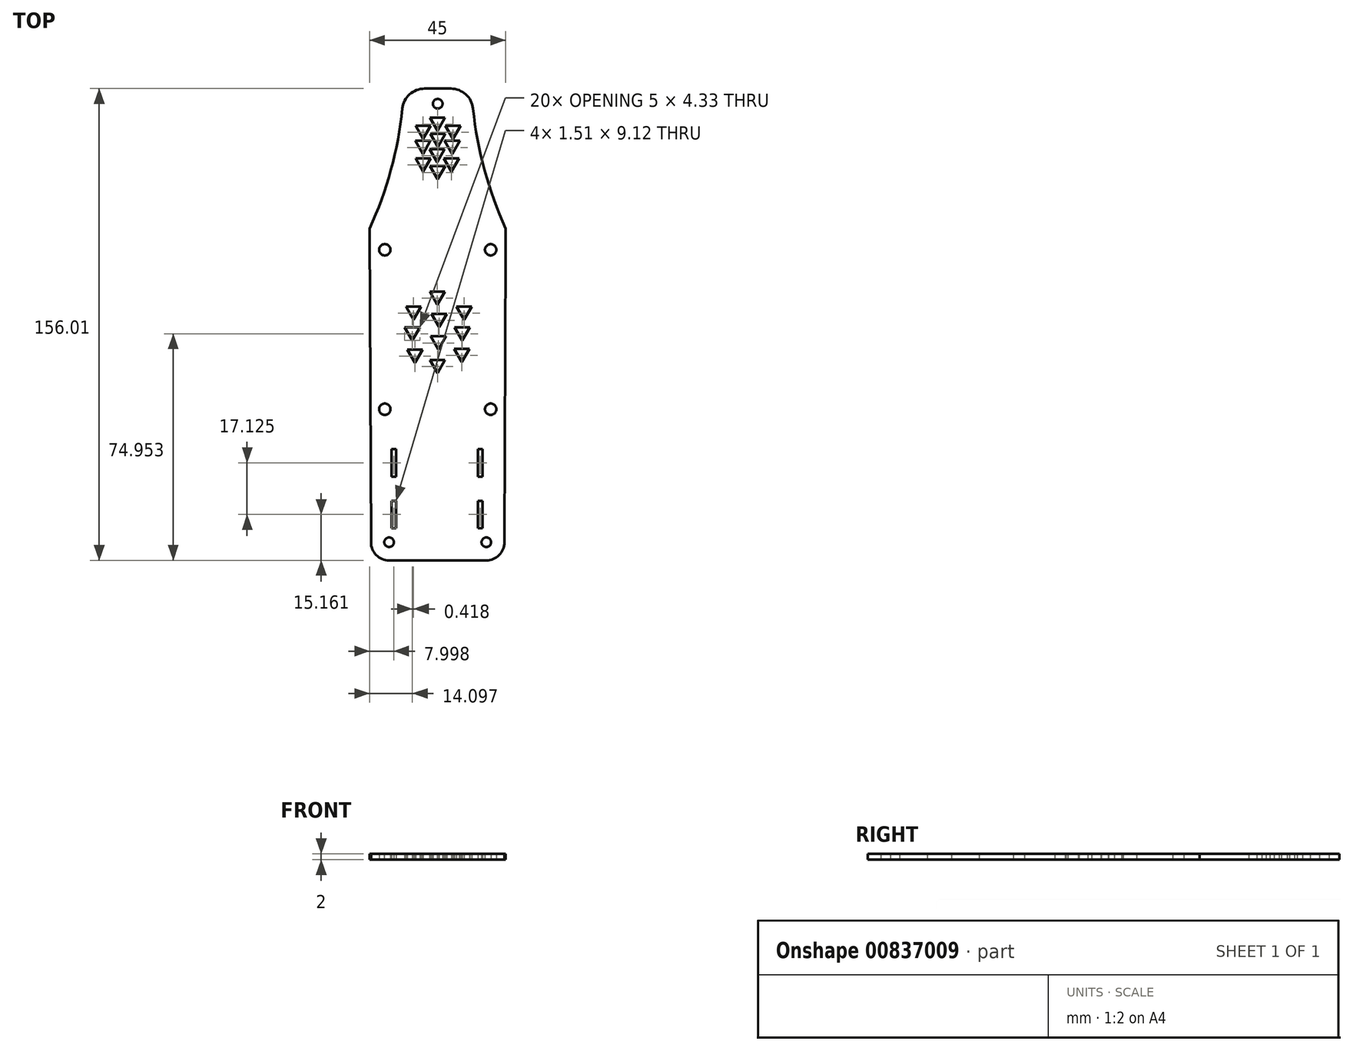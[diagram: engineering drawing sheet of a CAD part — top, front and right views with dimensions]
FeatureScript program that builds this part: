
annotation { "Feature Type Name" : "Feature", "Feature Type Description" : "" }
export const myFeature = defineFeature(function(context is Context, id is Id, definition is map)
    precondition{}
    {
        {
            var Q0;
            Q0=qCreatedBy(makeId("Top.planeOp"),FACE);
            var sketch = newSketch(context, id + "F0", { "sketchPlane" : qUnion([Q0])});
            skLineSegment(sketch, "E0.trimOffspring", {"start": v(9.73, 3.85) * mm, "end": v(9.72, 1.55) * mm});
            skArc(sketch, "E1.MirrorCS", {"start": v(-8.3, 74.97) * mm, "mid": v(-8.3, 74.97) * mm, "end": v(-8.3, 74.98) * mm});
            skLineSegment(sketch, "E2", {"start": v(-12.66, 82.35) * mm, "end": v(-8.3, 82.35) * mm});
            skLineSegment(sketch, "E3", {"start": v(9.84, 36.06) * mm, "end": v(9.84, 29.06) * mm});
            skLineSegment(sketch, "E4", {"start": v(9.84, 35.35) * mm, "end": v(9.84, 36.06) * mm});
            skArc(sketch, "E5", {"start": v(-0.97, 75.74) * mm, "mid": v(2.82, 55.46) * mm, "end": v(9.84, 36.06) * mm});
            skArc(sketch, "E6.filletArc", {"start": v(-0.97, 75.74) * mm, "mid": v(-3.37, 80.45) * mm, "end": v(-8.3, 82.35) * mm});
            skPoint(sketch, "E7.start.orphan", {"position": v(-17, 82.35) * mm});
            skLineSegment(sketch, "E8.MirrorCS", {"start": v(-12.66, 82.35) * mm, "end": v(-17, 82.35) * mm});
            skPoint(sketch, "E9.MirrorP", {"position": v(-17, 74.97) * mm});
            skPoint(sketch, "E10.MirrorP", {"position": v(-17, 74.98) * mm});
            skPoint(sketch, "E11.MirrorP", {"position": v(-8.3, 82.35) * mm});
            skCircle(sketch, "E12", {"center": v(-12.66, 77.35) * mm, "radius": 1.59 * mm});
            skArc(sketch, "E13.MirrorCS", {"start": v(-17, 74.97) * mm, "mid": v(-17, 74.97) * mm, "end": v(-17, 74.98) * mm});
            skLineSegment(sketch, "E14.MirrorCS", {"start": v(-35.16, 35.35) * mm, "end": v(-35.16, 36.06) * mm});
            skLineSegment(sketch, "E15.MirrorCS", {"start": v(-35.04, 3.85) * mm, "end": v(-35.04, 1.55) * mm});
            skArc(sketch, "E16.MirrorCS", {"start": v(-24.34, 75.74) * mm, "mid": v(-21.94, 80.45) * mm, "end": v(-17, 82.35) * mm});
            skArc(sketch, "E17.MirrorCS", {"start": v(-24.34, 75.74) * mm, "mid": v(-28.13, 55.46) * mm, "end": v(-35.16, 36.06) * mm});
            skLineSegment(sketch, "E18", {"start": v(-28.73, -73.66) * mm, "end": v(3.42, -73.66) * mm});
            skArc(sketch, "E19.filletArc", {"start": v(-34.73, -67.66) * mm, "mid": v(-32.97, -71.9) * mm, "end": v(-28.73, -73.66) * mm});
            skArc(sketch, "E20.filletArc", {"start": v(3.42, -73.66) * mm, "mid": v(7.66, -71.9) * mm, "end": v(9.42, -67.66) * mm});
            skCircle(sketch, "E21", {"center": v(3.42, -67.66) * mm, "radius": 1.59 * mm});
            skCircle(sketch, "E22", {"center": v(-28.73, -67.66) * mm, "radius": 1.59 * mm});
            skLineSegment(sketch, "E23.0", {"start": v(-10.1, 67.46) * mm, "end": v(-12.6, 63.13) * mm});
            skLineSegment(sketch, "E23.1", {"start": v(-12.6, 63.13) * mm, "end": v(-15.1, 67.46) * mm});
            skLineSegment(sketch, "E23.2", {"start": v(-15.1, 67.46) * mm, "end": v(-10.1, 67.46) * mm});
            skPoint(sketch, "E23.0.midPoint", {"position": v(-11.36, 65.3) * mm});
            skLineSegment(sketch, "E24.0", {"start": v(-15.07, 65.07) * mm, "end": v(-17.57, 60.74) * mm});
            skLineSegment(sketch, "E24.1", {"start": v(-17.57, 60.74) * mm, "end": v(-20.07, 65.07) * mm});
            skLineSegment(sketch, "E24.2", {"start": v(-20.07, 65.07) * mm, "end": v(-15.07, 65.07) * mm});
            skPoint(sketch, "E24.0.midPoint", {"position": v(-16.32, 62.9) * mm});
            skLineSegment(sketch, "E25.0", {"start": v(-10.36, 62.36) * mm, "end": v(-12.86, 58.03) * mm});
            skLineSegment(sketch, "E25.1", {"start": v(-12.86, 58.03) * mm, "end": v(-15.36, 62.36) * mm});
            skLineSegment(sketch, "E25.2", {"start": v(-15.36, 62.36) * mm, "end": v(-10.36, 62.36) * mm});
            skPoint(sketch, "E25.0.midPoint", {"position": v(-11.61, 60.2) * mm});
            skLineSegment(sketch, "E26.0", {"start": v(-5.4, 65.07) * mm, "end": v(-7.9, 60.74) * mm});
            skLineSegment(sketch, "E26.1", {"start": v(-7.9, 60.74) * mm, "end": v(-10.4, 65.07) * mm});
            skLineSegment(sketch, "E26.2", {"start": v(-10.4, 65.07) * mm, "end": v(-5.4, 65.07) * mm});
            skPoint(sketch, "E26.0.midPoint", {"position": v(-6.64, 62.9) * mm});
            skLineSegment(sketch, "E27.0", {"start": v(-5.1, 70.14) * mm, "end": v(-7.6, 65.81) * mm});
            skLineSegment(sketch, "E27.1", {"start": v(-7.6, 65.81) * mm, "end": v(-10.1, 70.14) * mm});
            skLineSegment(sketch, "E27.2", {"start": v(-10.1, 70.14) * mm, "end": v(-5.1, 70.14) * mm});
            skPoint(sketch, "E27.0.midPoint", {"position": v(-6.34, 67.98) * mm});
            skLineSegment(sketch, "E28.0", {"start": v(-10.22, 72.74) * mm, "end": v(-12.72, 68.41) * mm});
            skLineSegment(sketch, "E28.1", {"start": v(-12.72, 68.41) * mm, "end": v(-15.22, 72.74) * mm});
            skLineSegment(sketch, "E28.2", {"start": v(-15.22, 72.74) * mm, "end": v(-10.22, 72.74) * mm});
            skPoint(sketch, "E28.0.midPoint", {"position": v(-11.47, 70.58) * mm});
            skLineSegment(sketch, "E29.0", {"start": v(-15, 70.14) * mm, "end": v(-17.5, 65.81) * mm});
            skLineSegment(sketch, "E29.1", {"start": v(-17.5, 65.81) * mm, "end": v(-20, 70.14) * mm});
            skLineSegment(sketch, "E29.2", {"start": v(-20, 70.14) * mm, "end": v(-15, 70.14) * mm});
            skPoint(sketch, "E29.0.midPoint", {"position": v(-16.24, 67.98) * mm});
            skLineSegment(sketch, "E30.0", {"start": v(-5.63, 59.34) * mm, "end": v(-8.13, 55) * mm});
            skLineSegment(sketch, "E30.1", {"start": v(-8.13, 55) * mm, "end": v(-10.63, 59.34) * mm});
            skLineSegment(sketch, "E30.2", {"start": v(-10.63, 59.34) * mm, "end": v(-5.63, 59.34) * mm});
            skPoint(sketch, "E30.0.midPoint", {"position": v(-6.88, 57.17) * mm});
            skLineSegment(sketch, "E31.0", {"start": v(-15, 59.34) * mm, "end": v(-17.5, 55) * mm});
            skLineSegment(sketch, "E31.1", {"start": v(-17.5, 55) * mm, "end": v(-20, 59.34) * mm});
            skLineSegment(sketch, "E31.2", {"start": v(-20, 59.34) * mm, "end": v(-15, 59.34) * mm});
            skPoint(sketch, "E31.0.midPoint", {"position": v(-16.24, 57.17) * mm});
            skLineSegment(sketch, "E32.0", {"start": v(-10.2, 56.75) * mm, "end": v(-12.7, 52.42) * mm});
            skLineSegment(sketch, "E32.1", {"start": v(-12.7, 52.42) * mm, "end": v(-15.2, 56.75) * mm});
            skLineSegment(sketch, "E32.2", {"start": v(-15.2, 56.75) * mm, "end": v(-10.2, 56.75) * mm});
            skPoint(sketch, "E32.0.midPoint", {"position": v(-11.46, 54.58) * mm});
            skLineSegment(sketch, "E33.bottom", {"start": v(-27.92, -53.94) * mm, "end": v(-26.4, -53.94) * mm});
            skLineSegment(sketch, "E33.top", {"start": v(-27.92, -63.06) * mm, "end": v(-26.4, -63.06) * mm});
            skLineSegment(sketch, "E33.left", {"start": v(-27.92, -53.94) * mm, "end": v(-27.92, -63.06) * mm});
            skLineSegment(sketch, "E33.right", {"start": v(-26.4, -53.94) * mm, "end": v(-26.4, -63.06) * mm});
            skLineSegment(sketch, "E34.MirrorCS", {"start": v(2.12, -53.94) * mm, "end": v(2.12, -63.06) * mm});
            skLineSegment(sketch, "E35.MirrorCS", {"start": v(0.6, -53.94) * mm, "end": v(0.6, -63.06) * mm});
            skLineSegment(sketch, "E36.MirrorCS", {"start": v(2.12, -53.94) * mm, "end": v(0.6, -53.94) * mm});
            skLineSegment(sketch, "E37.MirrorCS", {"start": v(2.12, -63.06) * mm, "end": v(0.6, -63.06) * mm});
            skCircle(sketch, "E38", {"center": v(-30.16, 29.06) * mm, "radius": 1.88 * mm});
            skCircle(sketch, "E39.MirrorC", {"center": v(4.84, 29.06) * mm, "radius": 1.88 * mm});
            skLineSegment(sketch, "E40.MirrorCS", {"start": v(2.12, -36.81) * mm, "end": v(0.6, -36.81) * mm});
            skLineSegment(sketch, "E41.MirrorCS", {"start": v(-27.92, -45.94) * mm, "end": v(-26.4, -45.94) * mm});
            skLineSegment(sketch, "E42.MirrorCS", {"start": v(2.12, -45.94) * mm, "end": v(0.6, -45.94) * mm});
            skLineSegment(sketch, "E43.MirrorCS", {"start": v(-27.92, -36.81) * mm, "end": v(-26.4, -36.81) * mm});
            skLineSegment(sketch, "E44.MirrorCS", {"start": v(-27.92, -45.94) * mm, "end": v(-27.92, -36.81) * mm});
            skLineSegment(sketch, "E45.MirrorCS", {"start": v(2.12, -45.94) * mm, "end": v(2.12, -36.81) * mm});
            skLineSegment(sketch, "E46.MirrorCS", {"start": v(0.6, -45.94) * mm, "end": v(0.6, -36.81) * mm});
            skLineSegment(sketch, "E47.MirrorCS", {"start": v(-26.4, -45.94) * mm, "end": v(-26.4, -36.81) * mm});
            skCircle(sketch, "E48.MirrorC", {"center": v(-30.16, -23.67) * mm, "radius": 1.88 * mm});
            skCircle(sketch, "E49.MirrorC", {"center": v(4.84, -23.67) * mm, "radius": 1.88 * mm});
            skPoint(sketch, "E50", {"position": v(-12.66, 2.73) * mm});
            skLineSegment(sketch, "E51.0", {"start": v(-9.7, 7.89) * mm, "end": v(-12.2, 3.56) * mm});
            skLineSegment(sketch, "E51.1", {"start": v(-12.2, 3.56) * mm, "end": v(-14.7, 7.89) * mm});
            skLineSegment(sketch, "E51.2", {"start": v(-14.7, 7.89) * mm, "end": v(-9.7, 7.89) * mm});
            skPoint(sketch, "E51.0.midPoint", {"position": v(-10.96, 5.72) * mm});
            skLineSegment(sketch, "E52.0", {"start": v(-18.56, 3.46) * mm, "end": v(-21.06, -0.87) * mm});
            skLineSegment(sketch, "E52.1", {"start": v(-21.06, -0.87) * mm, "end": v(-23.56, 3.46) * mm});
            skLineSegment(sketch, "E52.2", {"start": v(-23.56, 3.46) * mm, "end": v(-18.56, 3.46) * mm});
            skPoint(sketch, "E52.0.midPoint", {"position": v(-19.81, 1.3) * mm});
            skLineSegment(sketch, "E53.0", {"start": v(-9.93, 0.43) * mm, "end": v(-12.43, -3.9) * mm});
            skLineSegment(sketch, "E53.1", {"start": v(-12.43, -3.9) * mm, "end": v(-14.93, 0.43) * mm});
            skLineSegment(sketch, "E53.2", {"start": v(-14.93, 0.43) * mm, "end": v(-9.93, 0.43) * mm});
            skPoint(sketch, "E53.0.midPoint", {"position": v(-11.18, -1.74) * mm});
            skLineSegment(sketch, "E54.0", {"start": v(-2.06, 3.46) * mm, "end": v(-4.56, -0.87) * mm});
            skLineSegment(sketch, "E54.1", {"start": v(-4.56, -0.87) * mm, "end": v(-7.06, 3.46) * mm});
            skLineSegment(sketch, "E54.2", {"start": v(-7.06, 3.46) * mm, "end": v(-2.06, 3.46) * mm});
            skPoint(sketch, "E54.0.midPoint", {"position": v(-3.3, 1.3) * mm});
            skLineSegment(sketch, "E55.0", {"start": v(-1.45, 10.32) * mm, "end": v(-3.95, 6) * mm});
            skLineSegment(sketch, "E55.1", {"start": v(-3.95, 6) * mm, "end": v(-6.45, 10.32) * mm});
            skLineSegment(sketch, "E55.2", {"start": v(-6.45, 10.32) * mm, "end": v(-1.45, 10.32) * mm});
            skPoint(sketch, "E55.0.midPoint", {"position": v(-2.7, 8.16) * mm});
            skLineSegment(sketch, "E56.0", {"start": v(-10.29, 15.23) * mm, "end": v(-12.79, 10.9) * mm});
            skLineSegment(sketch, "E56.1", {"start": v(-12.79, 10.9) * mm, "end": v(-15.29, 15.23) * mm});
            skLineSegment(sketch, "E56.2", {"start": v(-15.29, 15.23) * mm, "end": v(-10.29, 15.23) * mm});
            skPoint(sketch, "E56.0.midPoint", {"position": v(-11.54, 13.07) * mm});
            skLineSegment(sketch, "E57.0", {"start": v(-18.14, 10.27) * mm, "end": v(-20.64, 5.94) * mm});
            skLineSegment(sketch, "E57.1", {"start": v(-20.64, 5.94) * mm, "end": v(-23.14, 10.27) * mm});
            skLineSegment(sketch, "E57.2", {"start": v(-23.14, 10.27) * mm, "end": v(-18.14, 10.27) * mm});
            skPoint(sketch, "E57.0.midPoint", {"position": v(-19.4, 8.1) * mm});
            skLineSegment(sketch, "E58.0", {"start": v(-2.2, -3.7) * mm, "end": v(-4.7, -8.04) * mm});
            skLineSegment(sketch, "E58.1", {"start": v(-4.7, -8.04) * mm, "end": v(-7.2, -3.7) * mm});
            skLineSegment(sketch, "E58.2", {"start": v(-7.2, -3.7) * mm, "end": v(-2.2, -3.7) * mm});
            skPoint(sketch, "E58.0.midPoint", {"position": v(-3.46, -5.87) * mm});
            skLineSegment(sketch, "E59.0", {"start": v(-17.7, -3.96) * mm, "end": v(-20.2, -8.3) * mm});
            skLineSegment(sketch, "E59.1", {"start": v(-20.2, -8.3) * mm, "end": v(-22.7, -3.96) * mm});
            skLineSegment(sketch, "E59.2", {"start": v(-22.7, -3.96) * mm, "end": v(-17.7, -3.96) * mm});
            skPoint(sketch, "E59.0.midPoint", {"position": v(-18.95, -6.13) * mm});
            skLineSegment(sketch, "E60.0", {"start": v(-10.23, -7.4) * mm, "end": v(-12.73, -11.72) * mm});
            skLineSegment(sketch, "E60.1", {"start": v(-12.73, -11.72) * mm, "end": v(-15.23, -7.4) * mm});
            skLineSegment(sketch, "E60.2", {"start": v(-15.23, -7.4) * mm, "end": v(-10.23, -7.4) * mm});
            skPoint(sketch, "E60.0.midPoint", {"position": v(-11.48, -9.56) * mm});
            skLineSegment(sketch, "E61", {"start": v(-35.16, 35.35) * mm, "end": v(-34.73, -67.66) * mm});
            skLineSegment(sketch, "E62", {"start": v(9.84, 29.06) * mm, "end": v(9.42, -67.66) * mm});
            skSolve(sketch);
        }
        {
            var Q0;
            {var subQ1=sQuery(id+"F0.wireOp",EDGE,"E3");Q0=makeQuery(id+"F0.imprint","IMPRINT",FACE,{"disambiguationData":[TD([[makeQuery(id+"F0.imprint","IMPRINT",EDGE,{"derivedFrom":subQ1}),-1.0]])]});}
            var Q1;
            Q1 = qConstructionFilter(qBodyType(qCreatedBy(id + "F0" ,EDGE), BodyType.WIRE), ConstructionObject.NO);
            extrude(context, id + "F1", {"entities" : qUnion([Q0]), "surfaceEntities" : qUnion([Q1]), "depth" : 2 * mm, "offsetDistance" : 25.4 * mm});
        }
    });
